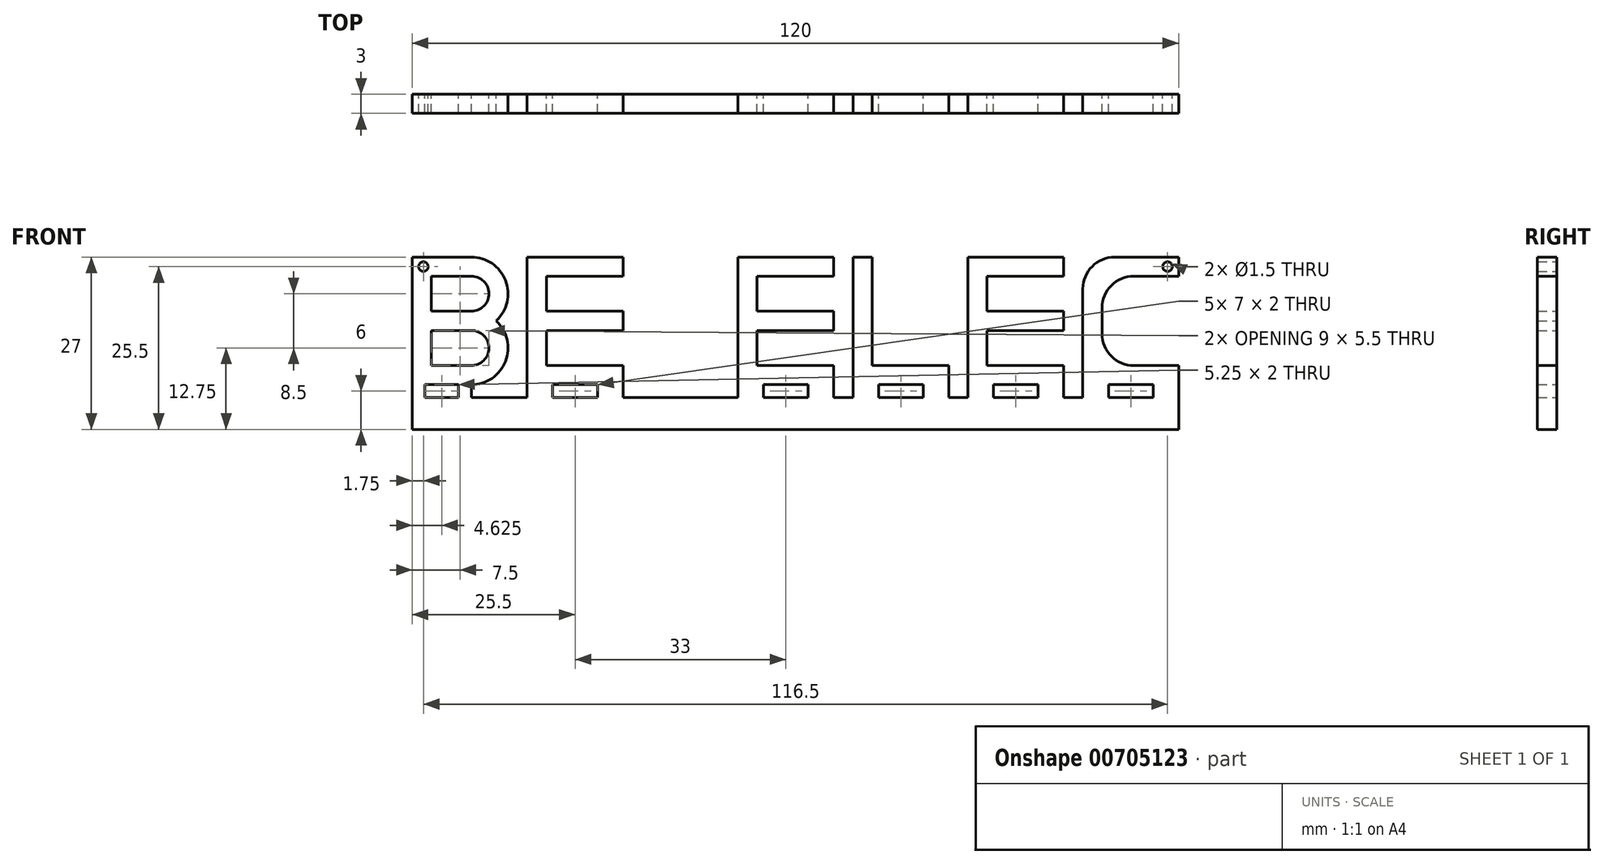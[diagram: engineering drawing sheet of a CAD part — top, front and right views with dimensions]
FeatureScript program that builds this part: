
annotation { "Feature Type Name" : "Feature", "Feature Type Description" : "" }
export const myFeature = defineFeature(function(context is Context, id is Id, definition is map)
    precondition{}
    {
        {
            var Q0;
            Q0=qCreatedBy(makeId("Front.planeOp"),FACE);
            var sketch = newSketch(context, id + "F0", { "sketchPlane" : qUnion([Q0])});
            skLineSegment(sketch, "E0.bottom", {"start": v(-56, 0) * mm, "end": v(-52.75, 0) * mm});
            skLineSegment(sketch, "E0.top", {"start": v(-60, -5) * mm, "end": v(60, -5) * mm});
            skLineSegment(sketch, "E0.left", {"start": v(-60, 0) * mm, "end": v(-60, -5) * mm});
            skLineSegment(sketch, "E0.right", {"start": v(60, 0) * mm, "end": v(60, -5) * mm});
            skLineSegment(sketch, "E1.top", {"start": v(-58, 2) * mm, "end": v(-56, 2) * mm});
            skLineSegment(sketch, "E1.left", {"start": v(-60, 0) * mm, "end": v(-60, 2) * mm});
            skLineSegment(sketch, "E1.right", {"start": v(-56, 0) * mm, "end": v(-56, 2) * mm, "construction": true});
            skLineSegment(sketch, "E2.bottom", {"start": v(-49, 2) * mm, "end": v(-45, 2) * mm, "construction": true});
            skLineSegment(sketch, "E2.left", {"start": v(-49, 2) * mm, "end": v(-49, 0) * mm, "construction": true});
            skLineSegment(sketch, "E2.right", {"start": v(-45, 2) * mm, "end": v(-45, 0) * mm, "construction": true});
            skLineSegment(sketch, "E3", {"start": v(-43.5, 0) * mm, "end": v(-43.5, 2.08) * mm, "construction": true});
            skLineSegment(sketch, "E4.MirrorCS", {"start": v(-42, 2) * mm, "end": v(-42, 0) * mm});
            skLineSegment(sketch, "E5.MirrorCS", {"start": v(-38, 2) * mm, "end": v(-38, 0) * mm});
            skLineSegment(sketch, "E6.MirrorCS", {"start": v(-31, 0) * mm, "end": v(-31, 2) * mm});
            skLineSegment(sketch, "E7.MirrorCS", {"start": v(-27, 0) * mm, "end": v(-27, 2) * mm});
            skLineSegment(sketch, "E8", {"start": v(-18, 0) * mm, "end": v(-18, 1.73) * mm, "construction": true});
            skLineSegment(sketch, "E9.MirrorCS", {"start": v(-9, 0) * mm, "end": v(-9, 2) * mm});
            skLineSegment(sketch, "E10.MirrorCS", {"start": v(-5, 0) * mm, "end": v(-5, 2) * mm});
            skLineSegment(sketch, "E11.MirrorCS", {"start": v(2, 2) * mm, "end": v(2, 0) * mm});
            skLineSegment(sketch, "E12.MirrorCS", {"start": v(2, 2) * mm, "end": v(6, 2) * mm});
            skLineSegment(sketch, "E13.MirrorCS", {"start": v(6, 2) * mm, "end": v(6, 0) * mm});
            skLineSegment(sketch, "E14.MirrorCS", {"start": v(9, 2) * mm, "end": v(9, 0) * mm});
            skLineSegment(sketch, "E15.MirrorCS", {"start": v(13, 2) * mm, "end": v(13, 0) * mm});
            skLineSegment(sketch, "E16.MirrorCS", {"start": v(20, 0) * mm, "end": v(20, 2) * mm});
            skLineSegment(sketch, "E17.MirrorCS", {"start": v(24, 0) * mm, "end": v(24, 2) * mm});
            skLineSegment(sketch, "E18.MirrorCS", {"start": v(24, 2) * mm, "end": v(20, 2) * mm});
            skLineSegment(sketch, "E19.MirrorCS", {"start": v(20, 0) * mm, "end": v(13, 0) * mm});
            skLineSegment(sketch, "E20", {"start": v(25.5, 0) * mm, "end": v(25.5, 2.16) * mm, "construction": true});
            skLineSegment(sketch, "E21.MirrorCS", {"start": v(56, 0) * mm, "end": v(56, 2) * mm});
            skLineSegment(sketch, "E22.MirrorCS", {"start": v(60, 2) * mm, "end": v(56, 2) * mm});
            skLineSegment(sketch, "E23.MirrorCS", {"start": v(60, 0) * mm, "end": v(60, 2) * mm});
            skLineSegment(sketch, "E24.MirrorCS", {"start": v(49, 2) * mm, "end": v(49, 0) * mm});
            skLineSegment(sketch, "E25.MirrorCS", {"start": v(45, 2) * mm, "end": v(45, 0) * mm});
            skLineSegment(sketch, "E26.MirrorCS", {"start": v(42, 2) * mm, "end": v(42, 0) * mm});
            skLineSegment(sketch, "E27.MirrorCS", {"start": v(38, 2) * mm, "end": v(42, 2) * mm});
            skLineSegment(sketch, "E28.MirrorCS", {"start": v(38, 2) * mm, "end": v(38, 0) * mm});
            skLineSegment(sketch, "E29.MirrorCS", {"start": v(27, 0) * mm, "end": v(27, 2) * mm});
            skLineSegment(sketch, "E30.MirrorCS", {"start": v(31, 0) * mm, "end": v(31, 2) * mm});
            skLineSegment(sketch, "E31.trimOffspring", {"start": v(49, 0) * mm, "end": v(56, 0) * mm});
            skLineSegment(sketch, "E32.trimOffspring", {"start": v(42, 0) * mm, "end": v(45, 0) * mm});
            skLineSegment(sketch, "E33.trimOffspring", {"start": v(31, 0) * mm, "end": v(38, 0) * mm});
            skPoint(sketch, "E34.orphan", {"position": v(24, 0) * mm});
            skLineSegment(sketch, "E35.trimOffspring", {"start": v(9, 0) * mm, "end": v(6, 0) * mm});
            skLineSegment(sketch, "E36.trimOffspring", {"start": v(2, 0) * mm, "end": v(-5, 0) * mm});
            skLineSegment(sketch, "E37.trimOffspring", {"start": v(-5, 0) * mm, "end": v(2, 0) * mm});
            skLineSegment(sketch, "E38.trimOffspring", {"start": v(13, 0) * mm, "end": v(20, 0) * mm});
            skLineSegment(sketch, "E39.trimOffspring", {"start": v(24, 0) * mm, "end": v(27, 0) * mm});
            skLineSegment(sketch, "E40.trimOffspring", {"start": v(-9, 0) * mm, "end": v(-27, 0) * mm});
            skLineSegment(sketch, "E41.trimOffspring", {"start": v(-27, 0) * mm, "end": v(-9, 0) * mm});
            skLineSegment(sketch, "E42.trimOffspring", {"start": v(-45, 0) * mm, "end": v(-42, 0) * mm});
            skLineSegment(sketch, "E43.trimOffspring", {"start": v(-42, 0) * mm, "end": v(-43.5, 0) * mm});
            skLineSegment(sketch, "E44.trimOffspring", {"start": v(-31, 0) * mm, "end": v(-38, 0) * mm});
            skLineSegment(sketch, "E45", {"start": v(-60, 2) * mm, "end": v(-60, 22) * mm});
            skLineSegment(sketch, "E46", {"start": v(-60, 22) * mm, "end": v(-50.75, 22) * mm});
            skLineSegment(sketch, "E47", {"start": v(-50.75, 19) * mm, "end": v(-57, 19) * mm});
            skLineSegment(sketch, "E48", {"start": v(-57, 19) * mm, "end": v(-57, 13.5) * mm});
            skLineSegment(sketch, "E49", {"start": v(-57, 13.5) * mm, "end": v(-50.75, 13.5) * mm});
            skLineSegment(sketch, "E50", {"start": v(-50.75, 10.5) * mm, "end": v(-57, 10.5) * mm});
            skLineSegment(sketch, "E51", {"start": v(-57, 10.5) * mm, "end": v(-57, 5) * mm});
            skLineSegment(sketch, "E52", {"start": v(-57, 5) * mm, "end": v(-50.75, 5) * mm});
            skLineSegment(sketch, "E53", {"start": v(-52.75, 2) * mm, "end": v(-56, 2) * mm});
            skArc(sketch, "E54", {"start": v(-50.75, 5) * mm, "mid": v(-48, 7.75) * mm, "end": v(-50.75, 10.5) * mm});
            skArc(sketch, "E55", {"start": v(-50.75, 2) * mm, "mid": v(-45.39, 5.67) * mm, "end": v(-46.88, 12) * mm});
            skArc(sketch, "E56", {"start": v(-50.75, 13.5) * mm, "mid": v(-48, 16.25) * mm, "end": v(-50.75, 19) * mm});
            skArc(sketch, "E57", {"start": v(-46.88, 12) * mm, "mid": v(-45.39, 18.33) * mm, "end": v(-50.75, 22) * mm});
            skLineSegment(sketch, "E58", {"start": v(-60, 12) * mm, "end": v(-56.88, 12) * mm, "construction": true});
            skLineSegment(sketch, "E59", {"start": v(-43.5, 2.08) * mm, "end": v(-43.5, 20.62) * mm, "construction": true});
            skLineSegment(sketch, "E60", {"start": v(-49, 0) * mm, "end": v(-45, 0) * mm});
            skLineSegment(sketch, "E61.left", {"start": v(-50.75, 2) * mm, "end": v(-50.75, 0) * mm});
            skLineSegment(sketch, "E61.right", {"start": v(-52.75, 2) * mm, "end": v(-52.75, 0) * mm});
            skLineSegment(sketch, "E62", {"start": v(-58, 2) * mm, "end": v(-58, 0) * mm});
            skLineSegment(sketch, "E63", {"start": v(-58, 0) * mm, "end": v(-56, 0) * mm});
            skLineSegment(sketch, "E64.trimOffspring", {"start": v(-50.75, 0) * mm, "end": v(-49, 0) * mm});
            skLineSegment(sketch, "E65.bottom", {"start": v(-39, 22) * mm, "end": v(-27, 22) * mm});
            skLineSegment(sketch, "E65.top", {"start": v(-39, 19) * mm, "end": v(-27, 19) * mm});
            skLineSegment(sketch, "E65.right", {"start": v(-27, 22) * mm, "end": v(-27, 19) * mm});
            skLineSegment(sketch, "E66.bottom", {"start": v(-39, 13.5) * mm, "end": v(-27, 13.5) * mm});
            skLineSegment(sketch, "E66.top", {"start": v(-39, 10.5) * mm, "end": v(-27, 10.5) * mm});
            skLineSegment(sketch, "E66.right", {"start": v(-27, 13.5) * mm, "end": v(-27, 10.5) * mm});
            skLineSegment(sketch, "E67.bottom", {"start": v(-39, 5) * mm, "end": v(-27, 5) * mm});
            skLineSegment(sketch, "E67.top", {"start": v(-38, 2) * mm, "end": v(-27, 2) * mm});
            skLineSegment(sketch, "E67.right", {"start": v(-27, 5) * mm, "end": v(-27, 2) * mm});
            skLineSegment(sketch, "E68.bottom", {"start": v(-42, 22) * mm, "end": v(-39, 22) * mm});
            skLineSegment(sketch, "E68.left", {"start": v(-42, 22) * mm, "end": v(-42, 2) * mm});
            skLineSegment(sketch, "E68.right", {"start": v(-39, 19) * mm, "end": v(-39, 13.5) * mm});
            skLineSegment(sketch, "E69", {"start": v(-42, 12) * mm, "end": v(-30.26, 12) * mm, "construction": true});
            skLineSegment(sketch, "E70.trimOffspring", {"start": v(-39, 10.5) * mm, "end": v(-39, 5) * mm});
            skLineSegment(sketch, "E71.bottom", {"start": v(-6, 22) * mm, "end": v(6, 22) * mm});
            skLineSegment(sketch, "E71.top", {"start": v(-6, 19) * mm, "end": v(6, 19) * mm});
            skLineSegment(sketch, "E71.right", {"start": v(6, 22) * mm, "end": v(6, 19) * mm});
            skLineSegment(sketch, "E72.bottom", {"start": v(-6, 13.5) * mm, "end": v(6, 13.5) * mm});
            skLineSegment(sketch, "E72.top", {"start": v(-6, 10.5) * mm, "end": v(6, 10.5) * mm});
            skLineSegment(sketch, "E72.right", {"start": v(6, 13.5) * mm, "end": v(6, 10.5) * mm});
            skLineSegment(sketch, "E73.bottom", {"start": v(-6, 5) * mm, "end": v(6, 5) * mm});
            skLineSegment(sketch, "E73.top", {"start": v(-5, 2) * mm, "end": v(6, 2) * mm});
            skLineSegment(sketch, "E73.right", {"start": v(6, 5) * mm, "end": v(6, 2) * mm});
            skLineSegment(sketch, "E74.bottom", {"start": v(-9, 22) * mm, "end": v(-6, 22) * mm});
            skLineSegment(sketch, "E74.left", {"start": v(-9, 22) * mm, "end": v(-9, 2) * mm});
            skLineSegment(sketch, "E74.right", {"start": v(-6, 19) * mm, "end": v(-6, 13.5) * mm});
            skLineSegment(sketch, "E75", {"start": v(-9, 12) * mm, "end": v(2.4, 12) * mm, "construction": true});
            skLineSegment(sketch, "E76.trimOffspring", {"start": v(-6, 10.5) * mm, "end": v(-6, 5) * mm});
            skLineSegment(sketch, "E77.bottom", {"start": v(12, 5) * mm, "end": v(24, 5) * mm});
            skLineSegment(sketch, "E77.top", {"start": v(13, 2) * mm, "end": v(24, 2) * mm});
            skLineSegment(sketch, "E77.right", {"start": v(24, 5) * mm, "end": v(24, 2) * mm});
            skLineSegment(sketch, "E78.bottom", {"start": v(9, 22) * mm, "end": v(12, 22) * mm});
            skLineSegment(sketch, "E78.left", {"start": v(9, 22) * mm, "end": v(9, 2) * mm});
            skLineSegment(sketch, "E78.right", {"start": v(12, 19) * mm, "end": v(12, 13.5) * mm});
            skLineSegment(sketch, "E79.trimOffspring", {"start": v(12, 10.5) * mm, "end": v(12, 5) * mm});
            skLineSegment(sketch, "E80.bottom", {"start": v(30, 22) * mm, "end": v(42, 22) * mm});
            skLineSegment(sketch, "E80.top", {"start": v(30, 19) * mm, "end": v(42, 19) * mm});
            skLineSegment(sketch, "E80.right", {"start": v(42, 22) * mm, "end": v(42, 19) * mm});
            skLineSegment(sketch, "E81.bottom", {"start": v(30, 13.5) * mm, "end": v(42, 13.5) * mm});
            skLineSegment(sketch, "E81.top", {"start": v(30, 10.5) * mm, "end": v(42, 10.5) * mm});
            skLineSegment(sketch, "E81.right", {"start": v(42, 13.5) * mm, "end": v(42, 10.5) * mm});
            skLineSegment(sketch, "E82.bottom", {"start": v(30, 5) * mm, "end": v(42, 5) * mm});
            skLineSegment(sketch, "E82.top", {"start": v(31, 2) * mm, "end": v(42, 2) * mm});
            skLineSegment(sketch, "E82.right", {"start": v(42, 5) * mm, "end": v(42, 2) * mm});
            skLineSegment(sketch, "E83.bottom", {"start": v(27, 22) * mm, "end": v(30, 22) * mm});
            skLineSegment(sketch, "E83.left", {"start": v(27, 22) * mm, "end": v(27, 2) * mm});
            skLineSegment(sketch, "E83.right", {"start": v(30, 19) * mm, "end": v(30, 13.5) * mm});
            skLineSegment(sketch, "E84", {"start": v(27, 12) * mm, "end": v(44.33, 12) * mm, "construction": true});
            skLineSegment(sketch, "E85.trimOffspring", {"start": v(30, 10.5) * mm, "end": v(30, 5) * mm});
            skLineSegment(sketch, "E86", {"start": v(12, 13.5) * mm, "end": v(12, 10.5) * mm});
            skLineSegment(sketch, "E87", {"start": v(12, 22) * mm, "end": v(12, 19) * mm});
            skLineSegment(sketch, "E88.bottom", {"start": v(48, 22) * mm, "end": v(60, 22) * mm});
            skLineSegment(sketch, "E88.top", {"start": v(48, 19) * mm, "end": v(60, 19) * mm});
            skLineSegment(sketch, "E88.right", {"start": v(60, 22) * mm, "end": v(60, 19) * mm});
            skLineSegment(sketch, "E89.bottom", {"start": v(48, 5) * mm, "end": v(60, 5) * mm});
            skLineSegment(sketch, "E89.top", {"start": v(49, 2) * mm, "end": v(60, 2) * mm});
            skLineSegment(sketch, "E89.right", {"start": v(60, 5) * mm, "end": v(60, 2) * mm});
            skLineSegment(sketch, "E90.bottom", {"start": v(45, 22) * mm, "end": v(48, 22) * mm});
            skLineSegment(sketch, "E90.left", {"start": v(45, 22) * mm, "end": v(45, 2) * mm});
            skLineSegment(sketch, "E90.right", {"start": v(48, 19) * mm, "end": v(48, 9.29) * mm});
            skLineSegment(sketch, "E91", {"start": v(45, 12) * mm, "end": v(55.46, 12) * mm, "construction": true});
            skLineSegment(sketch, "E92.trimOffspring", {"start": v(48, 6.29) * mm, "end": v(48, 5) * mm});
            skLineSegment(sketch, "E93", {"start": v(48, 9.29) * mm, "end": v(48, 6.29) * mm});
            skPoint(sketch, "E68.top.end.orphan", {"position": v(-39, 2) * mm});
            skPoint(sketch, "E74.top.end.orphan", {"position": v(-6, 2) * mm});
            skLineSegment(sketch, "E94.trimOffspring", {"start": v(6, 0) * mm, "end": v(9, 0) * mm});
            skPoint(sketch, "E95.orphan", {"position": v(12, 2) * mm});
            skPoint(sketch, "E83.top.end.orphan", {"position": v(30, 2) * mm});
            skPoint(sketch, "E90.top.end.orphan", {"position": v(48, 2) * mm});
            skLineSegment(sketch, "E96", {"start": v(60, 20.5) * mm, "end": v(53.5, 20.5) * mm, "construction": true});
            skLineSegment(sketch, "E97", {"start": v(-60, 20.5) * mm, "end": v(-54.87, 20.5) * mm, "construction": true});
            skCircle(sketch, "E98", {"center": v(-58.25, 20.5) * mm, "radius": 0.75 * mm});
            skCircle(sketch, "E99", {"center": v(58.25, 20.5) * mm, "radius": 0.75 * mm});
            skSolve(sketch);
        }
        {
            var Q0;
            Q0=makeQuery(id+"F0.imprint","IMPRINT",FACE,{"disambiguationData":[TD([[makeQuery(id+"F0.imprint","IMPRINT",EDGE,{"derivedFrom":sQuery(id+"F0.wireOp",EDGE,"E0.bottom")}),-1.0]])]});
            extrude(context, id + "F1", {"entities" : qUnion([Q0]), "depth" : 3 * mm, "offsetDistance" : 25 * mm});
        }
        {
            var Q0;
            Q0=makeQuery(id+"F1.opExtrude","SWEPT_EDGE",EDGE,{"disambiguationData":[OSD([sQuery(id+"F0.wireOp",EDGE,"E88.top"),sQuery(id+"F0.wireOp",EDGE,"E90.right")])]});
            var Q1;
            Q1=makeQuery(id+"F1.opExtrude","SWEPT_EDGE",EDGE,{"disambiguationData":[OSD([sQuery(id+"F0.wireOp",EDGE,"E89.bottom"),sQuery(id+"F0.wireOp",EDGE,"E92.trimOffspring")])]});
            var Q2;
            Q2=makeQuery(id+"F1.opExtrude","SWEPT_EDGE",EDGE,{"disambiguationData":[OSD([sQuery(id+"F0.wireOp",EDGE,"E90.bottom"),sQuery(id+"F0.wireOp",EDGE,"E90.left")])]});
            fillet(context, id + "F2", {"entities" : qUnion([Q0, Q1, Q2]), "radius" : 5 * mm, "tangentPropagation" : true, "allowEdgeOverflow" : false});
        }
    });
